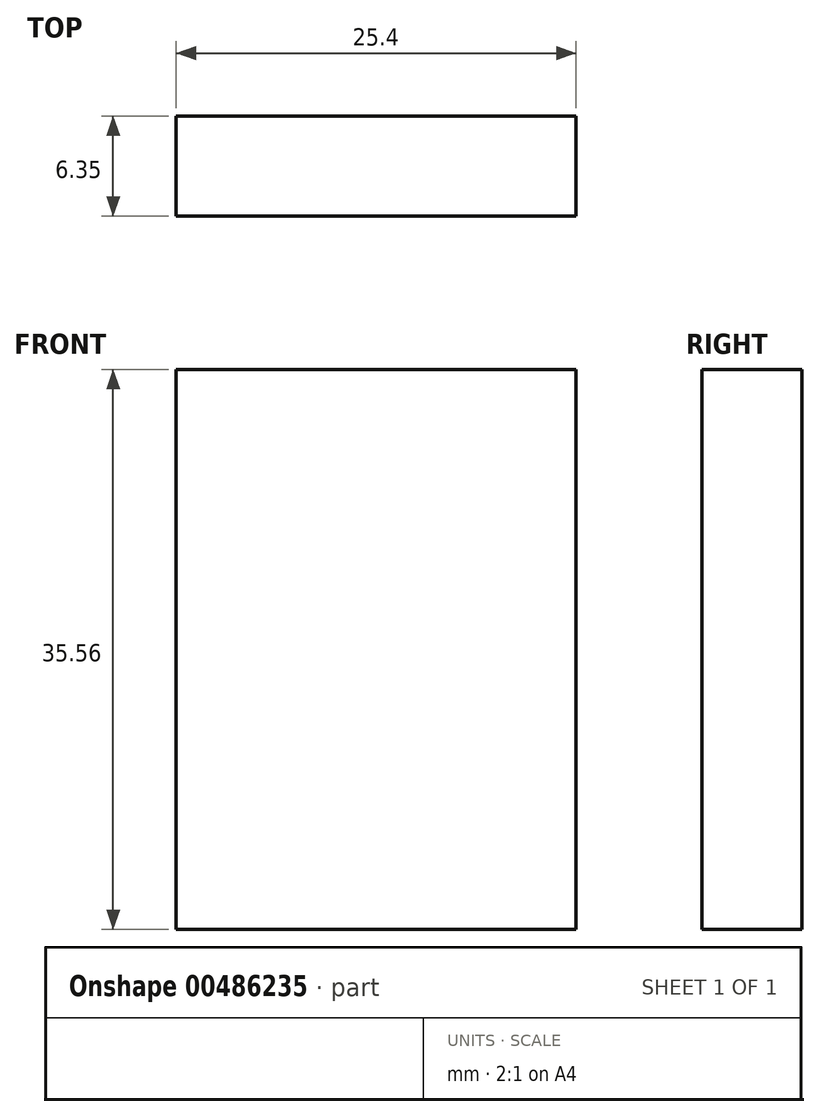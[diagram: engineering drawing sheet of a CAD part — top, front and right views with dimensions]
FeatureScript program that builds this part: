
annotation { "Feature Type Name" : "Feature", "Feature Type Description" : "" }
export const myFeature = defineFeature(function(context is Context, id is Id, definition is map)
    precondition{}
    {
        {
            var Q0;
            Q0=qCreatedBy(makeId("Front.planeOp"),FACE);
            var sketch = newSketch(context, id + "F0", { "sketchPlane" : qUnion([Q0])});
            skLineSegment(sketch, "E0.bottom", {"start": v(-12.7, 17.78) * mm, "end": v(12.7, 17.78) * mm});
            skLineSegment(sketch, "E0.top", {"start": v(-12.7, -17.78) * mm, "end": v(12.7, -17.78) * mm});
            skLineSegment(sketch, "E0.left", {"start": v(-12.7, 17.78) * mm, "end": v(-12.7, -17.78) * mm});
            skLineSegment(sketch, "E0.right", {"start": v(12.7, 17.78) * mm, "end": v(12.7, -17.78) * mm});
            skPoint(sketch, "E0.middle", {"position": v(0, 0) * mm});
            skSolve(sketch);
        }
        {
            var Q0;
            Q0 = qSketchRegion(id + "F0", true);
            extrude(context, id + "F1", {"entities" : qUnion([Q0]), "depth" : 6.35 * mm, "offsetDistance" : 25.4 * mm});
        }
    });
